# Revit family: BTSMP-LMO
name_source: partatom
category: Communication Devices
units: mm (PartAtom-declared; Revit-internal decimal feet)

## family parameters
Cut with Voids When Loaded = No
Host = Face
Maintain Annotation Orientation = No
OmniClass Number = 23.85.80.11.27
OmniClass Title = Lighting Controls
Part Type = Normal
Room Calculation Point = No
Round Connector Dimension = Use Diameter
Shared = Yes

## types (2) — shared parameters
Application = Parking Garage, Manufaturing, Site/Area, Warehouse, Gymnasiums, Office Space, Classroom
Assembly Code = D5090
Certifications = Conforms with UL STD 508, UL STD 244A
• IP65 Rated
Default Elevation = 48 "
Description = The Passive-Infrared Bluetooth sensor module, or BTMSP, is the newest series of the Control Solutions Bluetooth Sensor family. Perfect for architectural applications, it is smaller, more cost effective, seamlessly integrates with all luminaires and provides simple dimming control using the Control app.
Features = Passive Infrared (PIR) sensing technology provides excellent major
motion detection
• Wireless programming using HCS control mobile app
• 0-10V Dimming control
• Single/Dual motion sensor timer modes
• Daylight sensor with multiple daylight harvesting modes
• 360° and aisle coverage options
• Compact, discrete, low profile luminaire sensor
• Supports low temperature, water-tight and outdoor applications
Housing Material = Paint -  Matte White
Manufacturer = NX Lighting Controls
Model = Bluetooth® Low Mount Outdoor Sensor Module
Mounting = Maximum: up to 16 ft
Power Requirements = Low voltage, 12-32 VDC
Sensing Element = Metal-Nickel
Technology = Bluetooth, Daylight Harvesting, 0-10 V Dimming
Type Comments = Outdoor Sensor
URL = https://www.currentlighting.com
Warranty = 5-Years Warranty

## per-type parameters (varying)
| type | BTSMP-HMO-A |
| BTSMP-LMO | No |
| BTSMP-LMO-A | Yes |

## geometry (parser evidence)
native form markers: Sweep x6
no freeform markers — native parametric forms only
